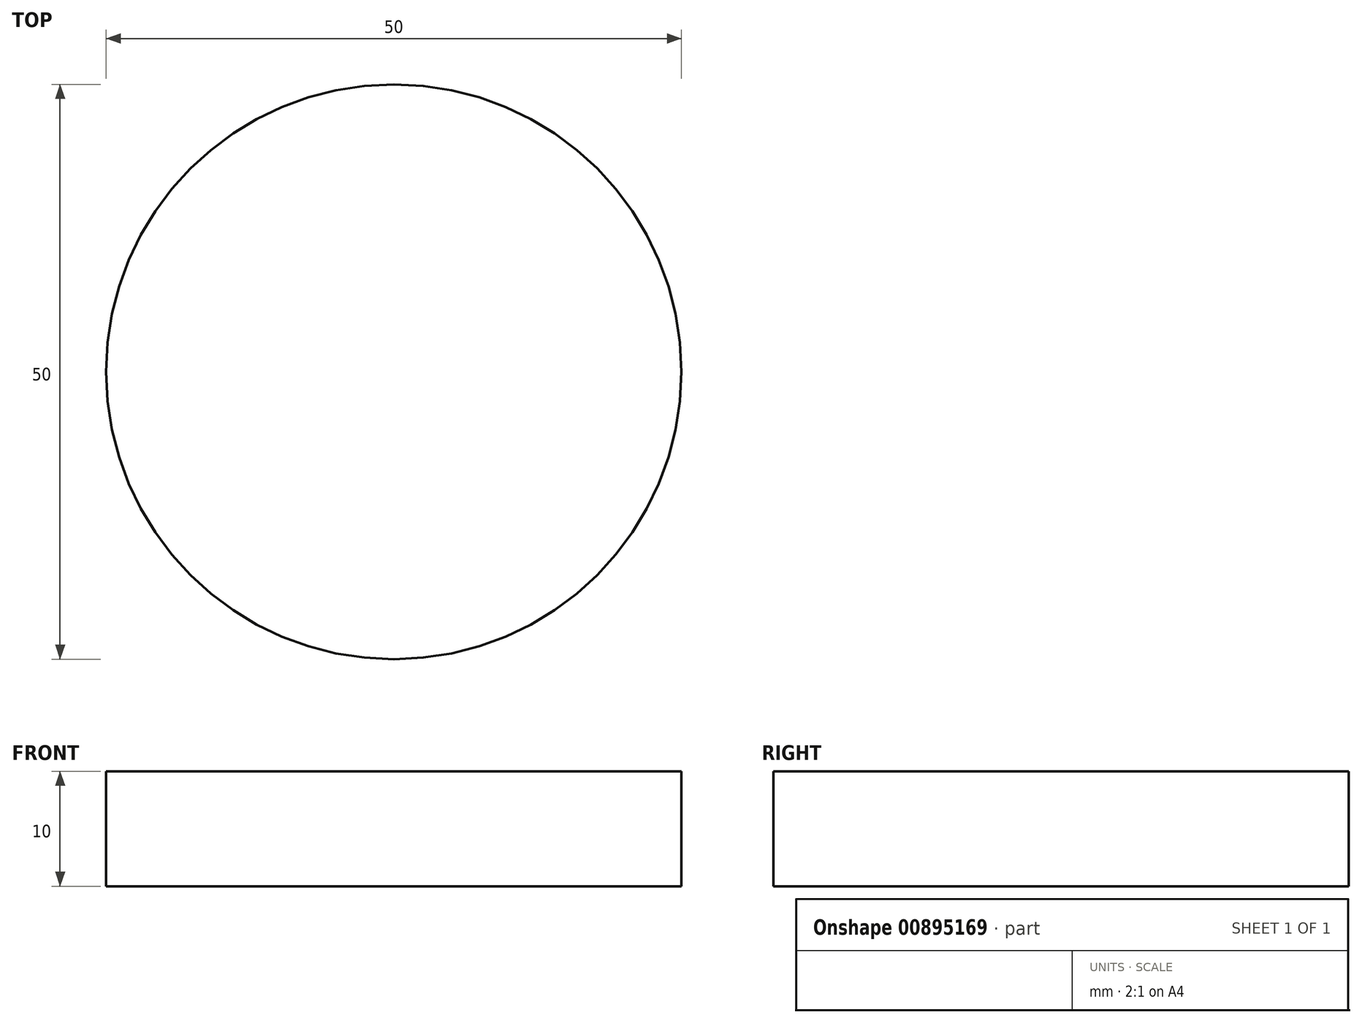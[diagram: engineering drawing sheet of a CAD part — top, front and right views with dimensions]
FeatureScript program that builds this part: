
annotation { "Feature Type Name" : "Feature", "Feature Type Description" : "" }
export const myFeature = defineFeature(function(context is Context, id is Id, definition is map)
    precondition{}
    {
        {
            var Q0;
            Q0=qCreatedBy(makeId("Top.planeOp"),FACE);
            var sketch = newSketch(context, id + "F0", { "sketchPlane" : qUnion([Q0])});
            skCircle(sketch, "E0", {"center": v(0, 0) * mm, "radius": 25 * mm});
            skSolve(sketch);
        }
        {
            var Q0;
            Q0=makeQuery(id+"F0.imprint","IMPRINT",FACE,{"disambiguationData":[TD([[makeQuery(id+"F0.imprint","IMPRINT",EDGE,{"derivedFrom":sQuery(id+"F0.wireOp",EDGE,"E0")}),1.0]])]});
            extrude(context, id + "F1", {"entities" : qUnion([Q0]), "depth" : 10 * mm, "offsetDistance" : 25.4 * mm});
        }
    });
